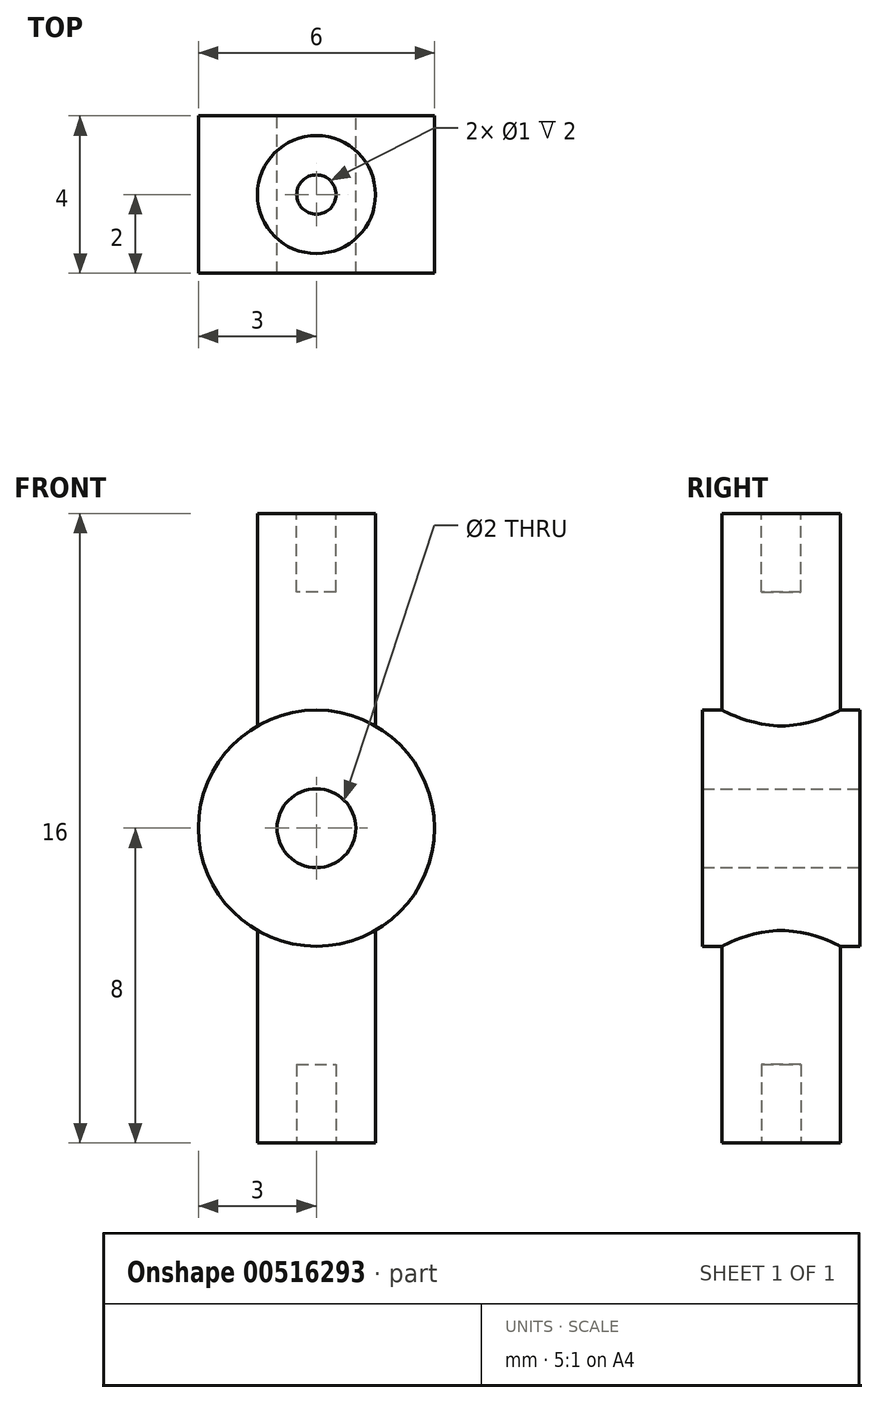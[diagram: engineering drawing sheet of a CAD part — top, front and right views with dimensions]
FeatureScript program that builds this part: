
annotation { "Feature Type Name" : "Feature", "Feature Type Description" : "" }
export const myFeature = defineFeature(function(context is Context, id is Id, definition is map)
    precondition{}
    {
        {
            var Q0;
            Q0=qCreatedBy(makeId("Top.planeOp"),FACE);
            var sketch = newSketch(context, id + "F0", { "sketchPlane" : qUnion([Q0])});
            skCircle(sketch, "E0", {"center": v(0, 0) * mm, "radius": 1.5 * mm});
            skSolve(sketch);
        }
        {
            var Q0;
            Q0 = qSketchRegion(id + "F0", true);
            extrude(context, id + "F1", {"entities" : qUnion([Q0]), "depth" : 16 * mm, "offsetDistance" : 25 * mm});
        }
        {
            var Q0;
            Q0=makeQuery(id+"F1.opExtrude","CAP_FACE",FACE,{"disambiguationData":[OSD([sQuery(id+"F0.wireOp",EDGE,"E0")])],"isStart":false});
            var sketch = newSketch(context, id + "F2", { "sketchPlane" : qUnion([Q0])});
            skCircle(sketch, "E1", {"center": v(0, 0) * mm, "radius": 0.5 * mm});
            skSolve(sketch);
        }
        {
            var Q0;
            Q0 = qSketchRegion(id + "F2", true);
            extrude(context, id + "F3", {"entities" : qUnion([Q0]), "operationType" : NewBodyOperationType.REMOVE, "oppositeDirection" : true, "depth" : 2 * mm, "offsetDistance" : 25 * mm});
        }
        {
            var Q0;
            Q0=makeQuery(id+"F1.opExtrude","CAP_FACE",FACE,{"disambiguationData":[OSD([sQuery(id+"F0.wireOp",EDGE,"E0")])],"isStart":true});
            var sketch = newSketch(context, id + "F4", { "sketchPlane" : qUnion([Q0])});
            skCircle(sketch, "E2", {"center": v(0, 0) * mm, "radius": 0.5 * mm});
            skSolve(sketch);
        }
        {
            var Q0;
            Q0 = qSketchRegion(id + "F4", true);
            extrude(context, id + "F5", {"entities" : qUnion([Q0]), "operationType" : NewBodyOperationType.REMOVE, "oppositeDirection" : true, "depth" : 2 * mm, "offsetDistance" : 25 * mm});
        }
        {
            var Q0;
            Q0=qCreatedBy(makeId("Front.planeOp"),FACE);
            var sketch = newSketch(context, id + "F6", { "sketchPlane" : qUnion([Q0])});
            skCircle(sketch, "E3", {"center": v(0, 8) * mm, "radius": 3 * mm});
            skCircle(sketch, "E4", {"center": v(0, 8) * mm, "radius": 1 * mm});
            skSolve(sketch);
        }
        {
            var Q0;
            Q0 = qSketchRegion(id + "F6", true);
            extrude(context, id + "F7", {"entities" : qUnion([Q0]), "operationType" : NewBodyOperationType.ADD, "depth" : 2 * mm, "offsetDistance" : 25 * mm, "hasSecondDirection" : true, "secondDirectionOppositeDirection" : true, "secondDirectionDepth" : 2 * mm});
        }
        {
            var Q0;
            Q0=qCreatedBy(makeId("Front.planeOp"),FACE);
            var sketch = newSketch(context, id + "F8", { "sketchPlane" : qUnion([Q0])});
            skCircle(sketch, "E5", {"center": v(0, 8) * mm, "radius": 1 * mm});
            skSolve(sketch);
        }
        {
            var Q0;
            Q0 = qSketchRegion(id + "F8", true);
            extrude(context, id + "F9", {"entities" : qUnion([Q0]), "operationType" : NewBodyOperationType.REMOVE, "oppositeDirection" : true, "depth" : 2 * mm, "offsetDistance" : 25 * mm, "hasSecondDirection" : true, "secondDirectionOppositeDirection" : false, "secondDirectionDepth" : 2 * mm});
        }
    });
